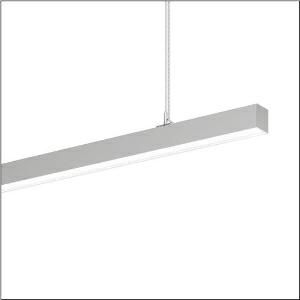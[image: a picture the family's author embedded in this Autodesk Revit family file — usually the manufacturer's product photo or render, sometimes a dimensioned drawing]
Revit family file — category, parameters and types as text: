
# Revit family: silica_r__21_51mx33tctds_657e
name_source: partatom
category: Lighting Fixtures
units: mm (PartAtom-declared; Revit-internal decimal feet)

## family parameters
Cut with Voids When Loaded = No
Host = Face
Light Source = No
Part Type = Normal
Room Calculation Point = No
Round Connector Dimension = Use Diameter
Shared = No

## types (1)
- --- (1 x LED, 14340 lm, 134.7 W, 6500K)
    Apparent Load = 135 VA
    CIE Flux Codes = 78 96 99 56 100
    Color Rendering = 80
    Color Temperature = 6500K
    Default Elevation = 1800 mm
    Description = Silica® 21, office luminaire, primary optical cover: prismatic diffuser, of PMMA, CAT 2 (L<= 3000cd/m²), light emission: direct/indirect distribution, primary light characteristic: symmetric, installation type: suspended mounting, LED, rated luminous flux: 14.340lm, luminous efficacy: 101lm/W, light colour: 8tw, colour temperature: 2700..6500K, control gear: ECG DALI, with terminal, 3+2-pole, max. 2.5mm², mains connection: 220..240V, AC, 50/60Hz, rated input power: 141.4W, luminaire housing, of aluminium, metallic grey (RAL 9006), length: 3.004mm, width: 53mm, height: 53mm, protection rating (complete): IP20, insulation class (complete): insulation class I (protective earthing), certification: CE, permissible operating ambient temperature: 0..+35°C, standard: EN 50419, packaging unit: 1 piece
    Height = 53 mm
    Lamp = 1 x LED
    Lamp Light Flux = 14340 lm
    Lamp Power = 134.7 W
    Lamp count = 1
    Length = 3004 mm
    Luminous efficacy = 106 lm/W
    Manufacturer = Siteco
    ModVariant = No
    Model = 51MX33TCTDS
    Mounting Place = Ceiling
    Mounting Type = Pendant
    Number of Poles = 1
    OnlyDefault = Yes
    Power Factor = 1
    Product Name = Silica® 21
    Product group = office luminaire | ceiling pendant
    ProductGroupID = 902
    Protection Class = Protection class I
    Protection Degree = IP 20
    RLX_Detail_Level = 1
    RLX_Emergency_Light_Flux = 0 lm
    RLX_Emergency_Type = 0
    RLX_Emergency_Type_DB = No
    RlxData = <blob elided: 20093 chars, md5=490682f0>
    Socket = socket
    Standby Power = 0 W
    System Light Flux = 14340 lm
    System Power = 135 W
    Type Comments = individual setting
    Type Image = l_1297747.jpg
    URL = http://relux.com
    VarID = @adj_071059
    Voltage = 0 V
    Weight = 0.00 kg
    Width = 53 mm

## geometry (parser evidence)
native form markers: Blend x4, Sweep x12
no freeform markers — native parametric forms only
